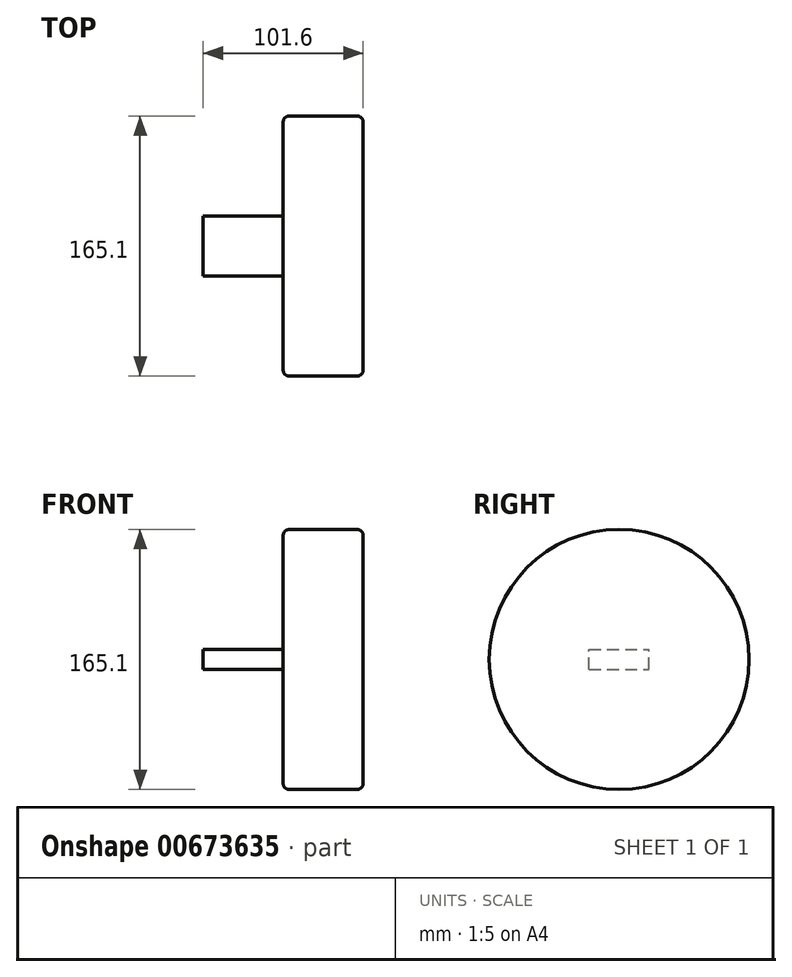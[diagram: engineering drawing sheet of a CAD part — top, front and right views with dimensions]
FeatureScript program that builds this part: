
annotation { "Feature Type Name" : "Feature", "Feature Type Description" : "" }
export const myFeature = defineFeature(function(context is Context, id is Id, definition is map)
    precondition{}
    {
        {
            var Q0;
            Q0=qCreatedBy(makeId("Right.planeOp"),FACE);
            var sketch = newSketch(context, id + "F0", { "sketchPlane" : qUnion([Q0])});
            skCircle(sketch, "E0", {"center": v(0, 0) * mm, "radius": 82.55 * mm});
            skSolve(sketch);
        }
        {
            var Q0;
            Q0=qSketchRegion(id+"F0",true);
            extrude(context, id + "F1", {"entities" : qUnion([Q0]), "depth" : 50.8 * mm, "offsetDistance" : 25.4 * mm});
        }
        {
            var Q0;
            Q0=makeQuery(id+"F1.opExtrude","CAP_EDGE",EDGE,{"disambiguationData":[OSD([sQuery(id+"F0.wireOp",EDGE,"E0")])],"isStart":false});
            var Q1;
            Q1=makeQuery(id+"F1.opExtrude","CAP_EDGE",EDGE,{"disambiguationData":[OSD([sQuery(id+"F0.wireOp",EDGE,"E0")])],"isStart":true});
            fillet(context, id + "F2", {"entities" : qUnion([Q0, Q1]), "radius" : 3.8 * mm, "tangentPropagation" : true, "allowEdgeOverflow" : false});
        }
        {
            var Q0;
            Q0=makeQuery(id+"F1.opExtrude","CAP_FACE",FACE,{"disambiguationData":[OSD([sQuery(id+"F0.wireOp",EDGE,"E0")])],"isStart":true});
            var sketch = newSketch(context, id + "F3", { "sketchPlane" : qUnion([Q0])});
            skLineSegment(sketch, "E1.bottom", {"start": v(19.05, -6.35) * mm, "end": v(-19.05, -6.35) * mm});
            skLineSegment(sketch, "E1.top", {"start": v(19.05, 6.35) * mm, "end": v(-19.05, 6.35) * mm});
            skLineSegment(sketch, "E1.left", {"start": v(19.05, -6.35) * mm, "end": v(19.05, 6.35) * mm});
            skLineSegment(sketch, "E1.right", {"start": v(-19.05, -6.35) * mm, "end": v(-19.05, 6.35) * mm});
            skPoint(sketch, "E1.middle", {"position": v(0, 0) * mm});
            skSolve(sketch);
        }
        {
            var Q0;
            Q0=makeQuery(id+"F3.imprint","IMPRINT",FACE,{"disambiguationData":[TD([[makeQuery(id+"F3.imprint","IMPRINT",EDGE,{"derivedFrom":sQuery(id+"F3.wireOp",EDGE,"E1.bottom")}),-1.0]])]});
            extrude(context, id + "F4", {"entities" : qUnion([Q0]), "operationType" : NewBodyOperationType.ADD, "depth" : 50.8 * mm, "offsetDistance" : 25.4 * mm});
        }
    });
